# Revit family: DARRAN - Six - Tables2
name_source: partatom
category: Furniture
units: mm (PartAtom-declared; Revit-internal decimal feet)

## family parameters
Always vertical = Yes
Cut with Voids When Loaded = No
OmniClass Number = 23.40.20.00
OmniClass Title = General Furniture and Specialties
Room Calculation Point = No
Shared = No
Work Plane-Based = No

## types (6) — shared parameters
Manufacturer = DARRAN
Top Corner Radius = 0' - 0 1/2"
URL = https://www.darran.com

## per-type parameters (varying)
| type | 3rd Leg | Base 2D | Base Ring | Leg Height | Leg Location | Leg Type 1 | Model | Table Height | Top Radius | Void Height |
| 20" Wide Occasional Table | Yes | 0' - 8 1/8" | No | 1' - 10 9/16" | 0' - 3 15/32" | Yes | SIX2024OT357 | 1' - 11 3/4" | 0' - 6 1/4" | 0' - 1" |
| 24" Wide Occasional Table | Yes | 0' - 9 27/32" | No | 1' - 10 9/16" | 0' - 5 3/16" | Yes | SIX2424OT357 | 1' - 11 3/4" | 0' - 8" | 0' - 1" |
| Low Occasional Table | Yes | 0' - 10" | No | 1' - 6 13/16" | 0' - 5 5/16" | Yes | SIX2420OT357 | 1' - 8" | 0' - 8" | 0' - 1" |
| Laptop Table | No | 0' - 8 23/32" | Yes | 1' - 10 29/32" | 0' - 4 3/32" | Yes | SIX2025LT356 | 2' - 0 3/32" | 0' - 6 1/4" | 0' - 3 1/4" |
| 18" H Coffee Table | Yes | 0' - 9 7/8" | No | 1' - 4 13/16" | 0' - 3 15/32" | No | SIX3618CT358 | 1' - 6" | 1' - 1 1/4" | 0' - 1" |
| 16.5" H Coffee Table | Yes | 1' - 0 27/32" | No | 1' - 3 5/16" | 0' - 6 13/32" | No | SIX4217CT358 | 1' - 4 1/2" | 1' - 4" | 0' - 1" |

## geometry (parser evidence)
native form markers: Sweep x9
no freeform markers — native parametric forms only
